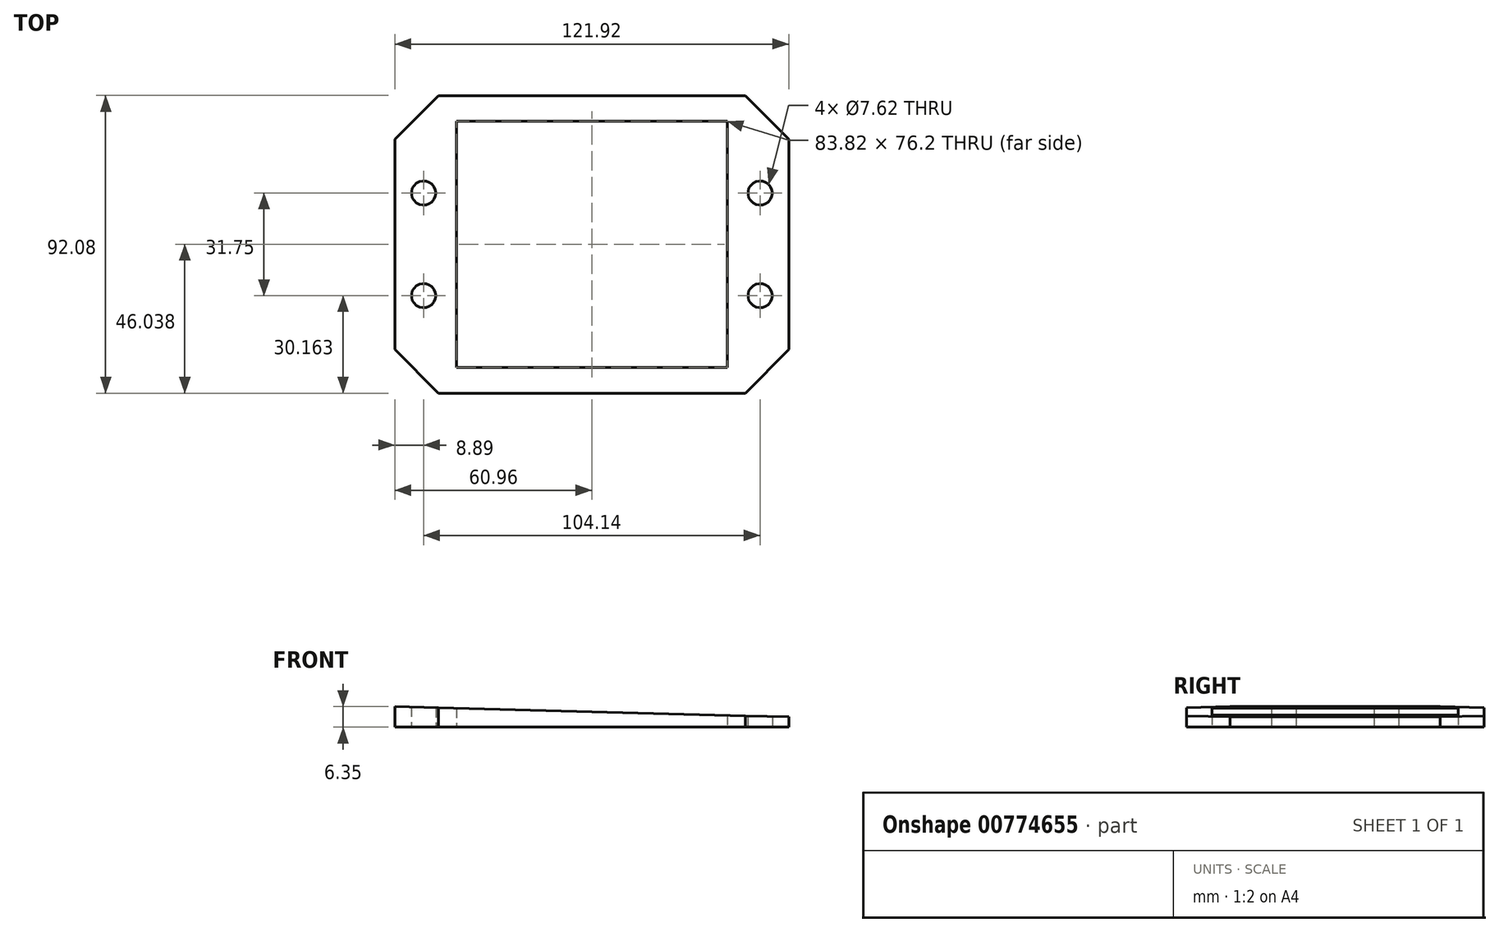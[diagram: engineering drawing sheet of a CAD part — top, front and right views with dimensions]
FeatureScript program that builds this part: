
annotation { "Feature Type Name" : "Feature", "Feature Type Description" : "" }
export const myFeature = defineFeature(function(context is Context, id is Id, definition is map)
    precondition{}
    {
        {
            var Q0;
            Q0=qCreatedBy(makeId("Front.planeOp"),FACE);
            var sketch = newSketch(context, id + "F0", { "sketchPlane" : qUnion([Q0])});
            skLineSegment(sketch, "E0", {"start": v(0, 0) * mm, "end": v(0, 6.35) * mm});
            skLineSegment(sketch, "E1", {"start": v(0, 6.35) * mm, "end": v(121.92, 3.17) * mm});
            skLineSegment(sketch, "E2", {"start": v(121.92, 3.17) * mm, "end": v(121.92, 0) * mm});
            skLineSegment(sketch, "E3", {"start": v(121.92, 0) * mm, "end": v(0, 0) * mm});
            skSolve(sketch);
        }
        {
            var Q0;
            Q0=makeQuery(id+"F0.imprint","IMPRINT",FACE,{"disambiguationData":[TD([[makeQuery(id+"F0.imprint","IMPRINT",EDGE,{"derivedFrom":sQuery(id+"F0.wireOp",EDGE,"E0")}),-1.0]])]});
            extrude(context, id + "F1", {"entities" : qUnion([Q0]), "depth" : -92.07 * mm, "offsetDistance" : 25.4 * mm});
        }
        {
            var Q0;
            Q0=qCreatedBy(makeId("Top.planeOp"),FACE);
            var sketch = newSketch(context, id + "F2", { "sketchPlane" : qUnion([Q0])});
            skCircle(sketch, "E4", {"center": v(8.9, 30.16) * mm, "radius": 3.81 * mm});
            skCircle(sketch, "E5", {"center": v(8.9, 61.91) * mm, "radius": 3.81 * mm});
            skCircle(sketch, "E6", {"center": v(113.03, 61.91) * mm, "radius": 3.81 * mm});
            skCircle(sketch, "E7", {"center": v(113.03, 30.16) * mm, "radius": 3.81 * mm});
            skLineSegment(sketch, "E8.bottom", {"start": v(19.05, 84.14) * mm, "end": v(102.87, 84.14) * mm});
            skLineSegment(sketch, "E8.top", {"start": v(19.05, 7.94) * mm, "end": v(102.87, 7.94) * mm});
            skLineSegment(sketch, "E8.left", {"start": v(19.05, 84.14) * mm, "end": v(19.05, 7.94) * mm});
            skLineSegment(sketch, "E8.right", {"start": v(102.87, 84.14) * mm, "end": v(102.87, 7.94) * mm});
            skLineSegment(sketch, "E9", {"start": v(0, 46.04) * mm, "end": v(121.92, 46.04) * mm, "construction": true});
            skLineSegment(sketch, "E10", {"start": v(60.96, 0) * mm, "end": v(60.96, 92.08) * mm, "construction": true});
            skLineSegment(sketch, "E11", {"start": v(0, 0) * mm, "end": v(0, 92.07) * mm});
            skLineSegment(sketch, "E12", {"start": v(0, 92.08) * mm, "end": v(121.92, 92.08) * mm});
            skLineSegment(sketch, "E13", {"start": v(121.92, 92.08) * mm, "end": v(121.92, 0) * mm});
            skLineSegment(sketch, "E14", {"start": v(121.92, 0) * mm, "end": v(0, 0) * mm});
            skLineSegment(sketch, "E15", {"start": v(108.45, 92.08) * mm, "end": v(121.92, 78.6) * mm});
            skLineSegment(sketch, "E16", {"start": v(108.45, 0) * mm, "end": v(121.92, 13.47) * mm});
            skLineSegment(sketch, "E17", {"start": v(13.47, 0) * mm, "end": v(0, 13.47) * mm});
            skLineSegment(sketch, "E18", {"start": v(0, 78.6) * mm, "end": v(13.47, 92.07) * mm});
            skLineSegment(sketch, "E19", {"start": v(13.47, 92.07) * mm, "end": v(0, 92.07) * mm});
            skLineSegment(sketch, "E20", {"start": v(108.45, 92.08) * mm, "end": v(121.92, 92.08) * mm});
            skLineSegment(sketch, "E21", {"start": v(121.92, 92.08) * mm, "end": v(121.92, 78.6) * mm});
            skLineSegment(sketch, "E22", {"start": v(121.92, 13.47) * mm, "end": v(121.92, 0) * mm});
            skLineSegment(sketch, "E23", {"start": v(121.92, 0) * mm, "end": v(108.45, 0) * mm});
            skLineSegment(sketch, "E24", {"start": v(13.47, 0) * mm, "end": v(0, 0) * mm});
            skLineSegment(sketch, "E25", {"start": v(0, 13.47) * mm, "end": v(0, 0) * mm});
            skSolve(sketch);
        }
        {
            var Q0;
            Q0=makeQuery(id+"F2.imprint","IMPRINT",FACE,{"disambiguationData":[TD([[makeQuery(id+"F2.imprint","IMPRINT",EDGE,{"derivedFrom":sQuery(id+"F2.wireOp",EDGE,"E5")}),1.0]])]});
            var Q1;
            Q1=makeQuery(id+"F2.imprint","IMPRINT",FACE,{"disambiguationData":[TD([[makeQuery(id+"F2.imprint","IMPRINT",EDGE,{"derivedFrom":sQuery(id+"F2.wireOp",EDGE,"E4")}),1.0]])]});
            var Q2;
            Q2=makeQuery(id+"F2.imprint","IMPRINT",FACE,{"disambiguationData":[TD([[makeQuery(id+"F2.imprint","IMPRINT",EDGE,{"derivedFrom":sQuery(id+"F2.wireOp",EDGE,"E7")}),1.0]])]});
            var Q3;
            Q3=makeQuery(id+"F2.imprint","IMPRINT",FACE,{"disambiguationData":[TD([[makeQuery(id+"F2.imprint","IMPRINT",EDGE,{"derivedFrom":sQuery(id+"F2.wireOp",EDGE,"E6")}),1.0]])]});
            var Q4;
            Q4=makeQuery(id+"F2.imprint","IMPRINT",FACE,{"disambiguationData":[TD([[makeQuery(id+"F2.imprint","IMPRINT",EDGE,{"derivedFrom":sQuery(id+"F2.wireOp",EDGE,"E8.bottom")}),-1.0]])]});
            var Q5;
            Q5=makeQuery(id+"F2.imprint","IMPRINT",FACE,{"disambiguationData":[TD([[makeQuery(id+"F2.imprint","IMPRINT",EDGE,{"derivedFrom":sQuery(id+"F2.wireOp",EDGE,"E15")}),1.0]])]});
            var Q6;
            {var subQ2=sQuery(id+"F2.wireOp",EDGE,"E18");Q6=makeQuery(id+"F2.imprint","IMPRINT",FACE,{"disambiguationData":[TD([[makeQuery(id+"F2.imprint","IMPRINT",EDGE,{"derivedFrom":subQ2}),1.0]])]});}
            var Q7;
            Q7=makeQuery(id+"F2.imprint","IMPRINT",FACE,{"disambiguationData":[TD([[makeQuery(id+"F2.imprint","IMPRINT",EDGE,{"derivedFrom":sQuery(id+"F2.wireOp",EDGE,"E17")}),1.0]])]});
            var Q8;
            Q8=makeQuery(id+"F2.imprint","IMPRINT",FACE,{"disambiguationData":[TD([[makeQuery(id+"F2.imprint","IMPRINT",EDGE,{"derivedFrom":sQuery(id+"F2.wireOp",EDGE,"E16")}),-1.0]])]});
            extrude(context, id + "F3", {"entities" : qUnion([Q0, Q1, Q2, Q3, Q4, Q5, Q6, Q7, Q8]), "operationType" : NewBodyOperationType.REMOVE, "depth" : 25.4 * mm, "offsetDistance" : 25.4 * mm});
        }
    });
